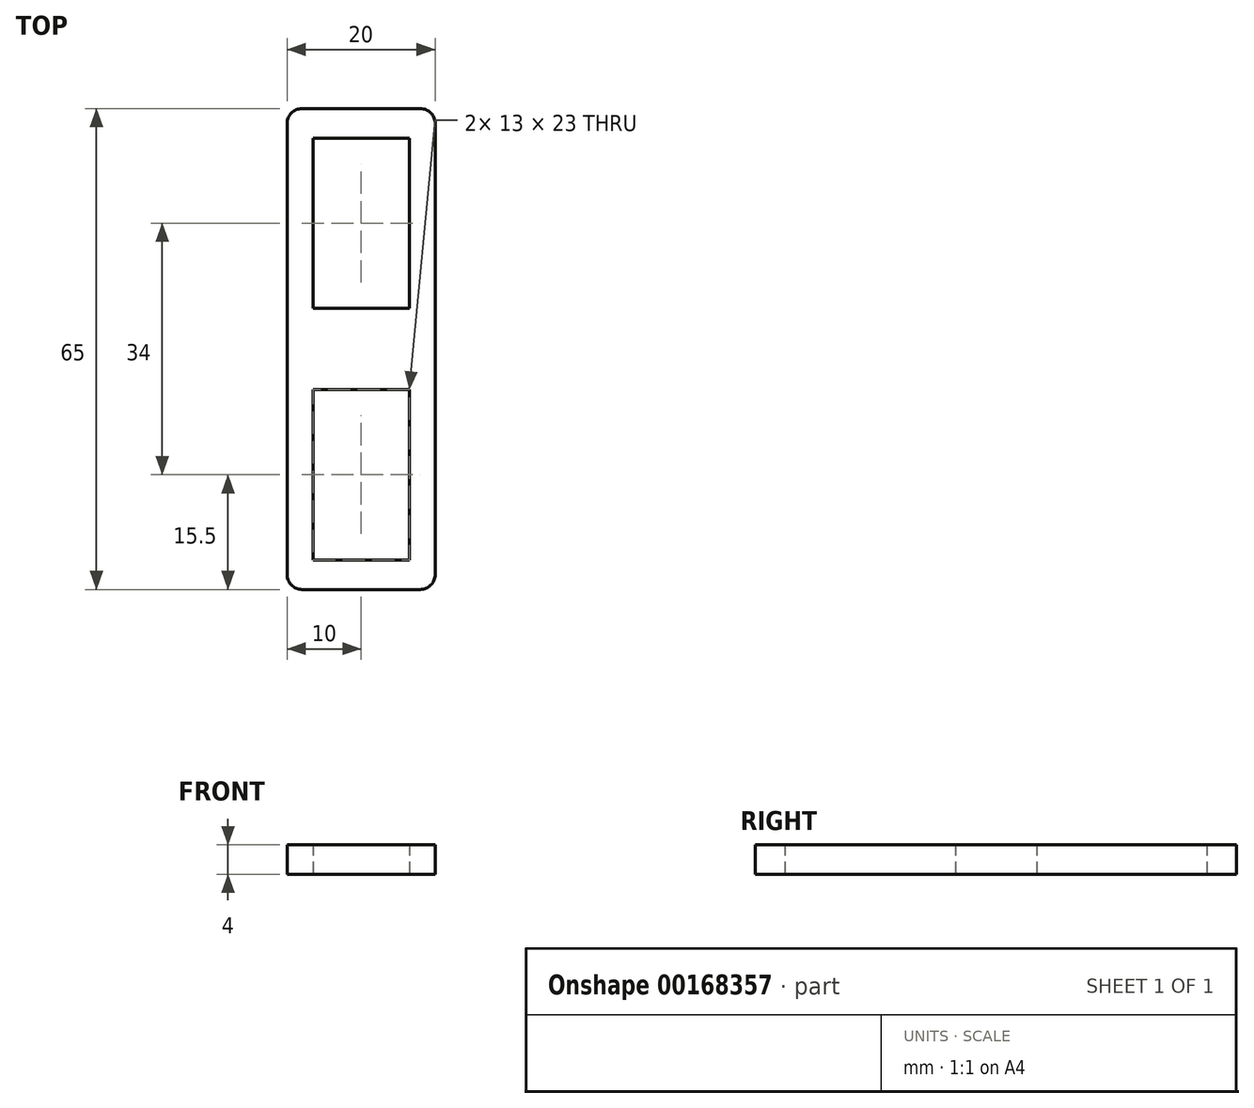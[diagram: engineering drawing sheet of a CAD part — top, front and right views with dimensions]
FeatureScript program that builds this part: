
annotation { "Feature Type Name" : "Feature", "Feature Type Description" : "" }
export const myFeature = defineFeature(function(context is Context, id is Id, definition is map)
    precondition{}
    {
        {
            var Q0;
            Q0=qCreatedBy(makeId("Top.planeOp"),FACE);
            var sketch = newSketch(context, id + "F0", { "sketchPlane" : qUnion([Q0])});
            skLineSegment(sketch, "E0.bottom", {"start": v(10, -32.5) * mm, "end": v(-10, -32.5) * mm});
            skLineSegment(sketch, "E0.top", {"start": v(10, 32.5) * mm, "end": v(-10, 32.5) * mm});
            skLineSegment(sketch, "E0.left", {"start": v(10, -32.5) * mm, "end": v(10, 32.5) * mm});
            skLineSegment(sketch, "E0.right", {"start": v(-10, -32.5) * mm, "end": v(-10, 32.5) * mm});
            skPoint(sketch, "E0.middle", {"position": v(0, 0) * mm});
            skPoint(sketch, "E1.middle", {"position": v(0, 18.97) * mm});
            skLineSegment(sketch, "E2.bottom", {"start": v(6.5, -5.5) * mm, "end": v(-6.5, -5.5) * mm});
            skLineSegment(sketch, "E2.top", {"start": v(6.5, -28.5) * mm, "end": v(-6.5, -28.5) * mm});
            skLineSegment(sketch, "E2.left", {"start": v(6.5, -5.5) * mm, "end": v(6.5, -28.5) * mm});
            skLineSegment(sketch, "E2.right", {"start": v(-6.5, -5.5) * mm, "end": v(-6.5, -28.5) * mm});
            skPoint(sketch, "E2.middle", {"position": v(0, -17) * mm});
            skLineSegment(sketch, "E3.MirrorCS", {"start": v(6.5, 5.5) * mm, "end": v(6.5, 28.5) * mm});
            skLineSegment(sketch, "E4.MirrorCS", {"start": v(6.5, 5.5) * mm, "end": v(-6.5, 5.5) * mm});
            skLineSegment(sketch, "E5.MirrorCS", {"start": v(-6.5, 5.5) * mm, "end": v(-6.5, 28.5) * mm});
            skLineSegment(sketch, "E6.MirrorCS", {"start": v(6.5, 28.5) * mm, "end": v(-6.5, 28.5) * mm});
            skPoint(sketch, "E7", {"position": v(0, -30.5) * mm});
            skPoint(sketch, "E7.positionSnap0", {"position": v(0, -32.5) * mm});
            skPoint(sketch, "E8.MirrorP", {"position": v(0, 30.5) * mm});
            skPoint(sketch, "E9", {"position": v(0, -5.5) * mm});
            skPoint(sketch, "E10", {"position": v(0, -3) * mm});
            skPoint(sketch, "E11.MirrorP", {"position": v(0, 3) * mm});
            skSolve(sketch);
        }
        {
            var Q0;
            Q0=makeQuery(id+"F0.imprint","IMPRINT",FACE,{"disambiguationData":[TD([[makeQuery(id+"F0.imprint","IMPRINT",EDGE,{"derivedFrom":sQuery(id+"F0.wireOp",EDGE,"E0.bottom")}),-1.0]])]});
            extrude(context, id + "F1", {"entities" : qUnion([Q0]), "depth" : 4 * mm});
        }
        {
            var Q0;
            Q0=makeQuery(id+"F1.opExtrude","SWEPT_EDGE",EDGE,{"disambiguationData":[OSD([sQuery(id+"F0.wireOp",EDGE,"E0.bottom"),sQuery(id+"F0.wireOp",EDGE,"E0.right")])]});
            var Q1;
            Q1=makeQuery(id+"F1.opExtrude","SWEPT_EDGE",EDGE,{"disambiguationData":[OSD([sQuery(id+"F0.wireOp",EDGE,"E0.bottom"),sQuery(id+"F0.wireOp",EDGE,"E0.left")])]});
            var Q2;
            Q2=makeQuery(id+"F1.opExtrude","SWEPT_EDGE",EDGE,{"disambiguationData":[OSD([sQuery(id+"F0.wireOp",EDGE,"E0.top"),sQuery(id+"F0.wireOp",EDGE,"E0.right")])]});
            var Q3;
            Q3=makeQuery(id+"F1.opExtrude","SWEPT_EDGE",EDGE,{"disambiguationData":[OSD([sQuery(id+"F0.wireOp",EDGE,"E0.top"),sQuery(id+"F0.wireOp",EDGE,"E0.left")])]});
            fillet(context, id + "F2", {"entities" : qUnion([Q0, Q1, Q2, Q3]), "radius" : 2 * mm, "tangentPropagation" : true, "allowEdgeOverflow" : false});
        }
    });
